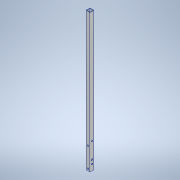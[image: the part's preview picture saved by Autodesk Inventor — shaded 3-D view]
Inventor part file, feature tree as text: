
AUTODESK INVENTOR PART (.ipt)
format: ipt  version: 2020.3 (Build 243373000, 373)  size: 151,040 bytes
history: native  units: mm
features: sketch x5, hole x3, extrude x2, other x1
ambient origin geometry x8: Origin, YZ Plane, XZ Plane, XY Plane, X Axis, Y Axis, Z Axis, Center Point
bodies: Body1 (feature_tree)
feature tree (11):
  other  "ソリッド1"
  extrude  "押し出し1"  Depth=9.0mm
  hole  "穴1"  [1 undecoded]
  hole  "穴2"  [1 undecoded]
  hole  "穴3"  [1 undecoded]
  extrude  "押し出し2"  Depth=1.2mm
  sketch  "スケッチ1"
  sketch  "スケッチ2"
  sketch  "スケッチ3"
  sketch  "スケッチ4"
  sketch  "スケッチ5"
note: 3 required parameter values undecoded (feature->parameter linkage not recoverable at this tier; creation-order binding heuristic only, values carry confidence <= 0.55)
